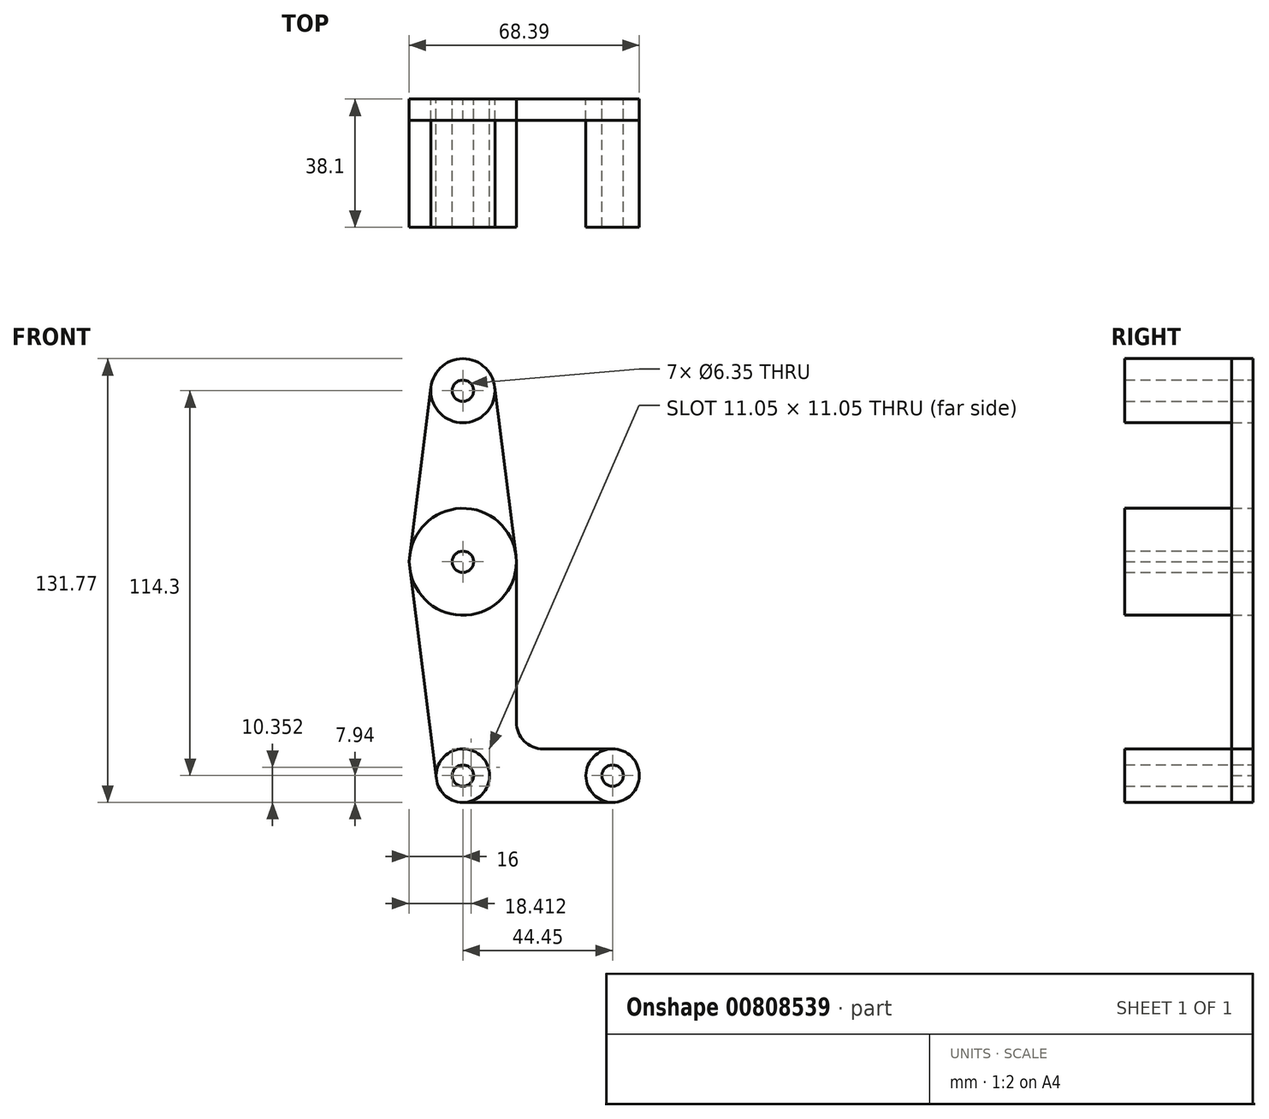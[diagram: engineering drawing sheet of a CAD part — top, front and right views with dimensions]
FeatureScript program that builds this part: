
annotation { "Feature Type Name" : "Feature", "Feature Type Description" : "" }
export const myFeature = defineFeature(function(context is Context, id is Id, definition is map)
    precondition{}
    {
        {
            var Q0;
            Q0=qCreatedBy(makeId("Front.planeOp"),FACE);
            var sketch = newSketch(context, id + "F0", { "sketchPlane" : qUnion([Q0])});
            skCircle(sketch, "E0", {"center": v(0, 0) * mm, "radius": 15.88 * mm});
            skLineSegment(sketch, "E1", {"start": v(0, 0) * mm, "end": v(0, -63.5) * mm});
            skLineSegment(sketch, "E2", {"start": v(0, 0) * mm, "end": v(0, 50.8) * mm});
            skCircle(sketch, "E3", {"center": v(0, 50.8) * mm, "radius": 9.53 * mm});
            skCircle(sketch, "E4", {"center": v(0, -63.5) * mm, "radius": 7.94 * mm});
            skCircle(sketch, "E5", {"center": v(0, 0) * mm, "radius": 3.18 * mm});
            skCircle(sketch, "E6", {"center": v(0, 50.8) * mm, "radius": 3.18 * mm});
            skCircle(sketch, "E7", {"center": v(0, -63.5) * mm, "radius": 3.18 * mm});
            skLineSegment(sketch, "E8", {"start": v(0, -63.5) * mm, "end": v(44.45, -63.5) * mm});
            skCircle(sketch, "E9", {"center": v(44.45, -63.5) * mm, "radius": 7.94 * mm});
            skCircle(sketch, "E10", {"center": v(44.45, -63.5) * mm, "radius": 3.18 * mm});
            skLineSegment(sketch, "E11", {"start": v(44.45, -55.56) * mm, "end": v(23.81, -55.56) * mm});
            skLineSegment(sketch, "E12", {"start": v(-9.45, 52) * mm, "end": v(-16, 0) * mm});
            skLineSegment(sketch, "E13", {"start": v(15.88, 0) * mm, "end": v(15.88, -47.62) * mm});
            skLineSegment(sketch, "E14", {"start": v(-16, 0) * mm, "end": v(-7.88, -64.5) * mm});
            skLineSegment(sketch, "E15", {"start": v(9.45, 52) * mm, "end": v(16, 0) * mm});
            skLineSegment(sketch, "E16", {"start": v(0, -71.44) * mm, "end": v(44.45, -71.44) * mm});
            skPoint(sketch, "E17.visualSharp", {"position": v(15.88, -55.56) * mm});
            skArc(sketch, "E17.filletArc", {"start": v(15.88, -47.62) * mm, "mid": v(18.2, -53.24) * mm, "end": v(23.81, -55.56) * mm});
            skSolve(sketch);
        }
        {
            var Q0;
            {var subQ0=sQuery(id+"F0.wireOp",EDGE,"E12");var subQ1=sQuery(id+"F0.wireOp",EDGE,"E0");var subQ2=makeQuery(id+"F0.imprint","INTERSECT",VERTEX,{"derivedFrom":[subQ1,subQ0]});Q0=makeQuery(id+"F0.imprint","IMPRINT",FACE,{"disambiguationData":[TD([[makeQuery(id+"F0.imprint","IMPRINT",EDGE,{"disambiguationData":[TD([[subQ2,-1.0]])],"derivedFrom":subQ1}),-1.0]])]});}
            var Q1;
            Q1=makeQuery(id+"F0.imprint","IMPRINT",FACE,{"disambiguationData":[TD([[makeQuery(id+"F0.imprint","IMPRINT",EDGE,{"derivedFrom":sQuery(id+"F0.wireOp",EDGE,"E6")}),-1.0]])]});
            var Q2;
            Q2=makeQuery(id+"F0.imprint","IMPRINT",FACE,{"disambiguationData":[TD([[makeQuery(id+"F0.imprint","IMPRINT",EDGE,{"derivedFrom":sQuery(id+"F0.wireOp",EDGE,"E10")}),-1.0]])]});
            var Q3;
            {var subQ0=sQuery(id+"F0.wireOp",EDGE,"E4");var subQ3=sQuery(id+"F0.wireOp",EDGE,"E1");var subQ4=makeQuery(id+"F0.imprint","INTERSECT",VERTEX,{"derivedFrom":[subQ3,subQ0]});Q3=makeQuery(id+"F0.imprint","IMPRINT",FACE,{"disambiguationData":[TD([[makeQuery(id+"F0.imprint","IMPRINT",EDGE,{"disambiguationData":[TD([[subQ4,-1.0]])],"derivedFrom":subQ3}),-1.0]])]});}
            var Q4;
            {var subQ0=sQuery(id+"F0.wireOp",EDGE,"E4");var subQ1=sQuery(id+"F0.wireOp",EDGE,"E1");var subQ2=makeQuery(id+"F0.imprint","INTERSECT",VERTEX,{"derivedFrom":[subQ1,subQ0]});Q4=makeQuery(id+"F0.imprint","IMPRINT",FACE,{"disambiguationData":[TD([[makeQuery(id+"F0.imprint","IMPRINT",EDGE,{"disambiguationData":[TD([[subQ2,-1.0]])],"derivedFrom":subQ1}),1.0]])]});}
            var Q5;
            {var subQ1=sQuery(id+"F0.wireOp",EDGE,"E0");var subQ9=makeQuery(id+"F0.imprint","INTERSECT",VERTEX,{"derivedFrom":[subQ1,sQuery(id+"F0.wireOp",EDGE,"E13")]});Q5=makeQuery(id+"F0.imprint","IMPRINT",FACE,{"disambiguationData":[TD([[makeQuery(id+"F0.imprint","IMPRINT",EDGE,{"disambiguationData":[TD([[subQ9,-1.0]])],"derivedFrom":subQ1}),1.0]])]});}
            var Q6;
            {var subQ0=sQuery(id+"F0.wireOp",EDGE,"E0");var subQ4=makeQuery(id+"F0.imprint","INTERSECT",VERTEX,{"derivedFrom":[subQ0,sQuery(id+"F0.wireOp",EDGE,"E12")]});Q6=makeQuery(id+"F0.imprint","IMPRINT",FACE,{"disambiguationData":[TD([[makeQuery(id+"F0.imprint","IMPRINT",EDGE,{"disambiguationData":[TD([[subQ4,1.0]])],"derivedFrom":subQ0}),1.0]])]});}
            extrude(context, id + "F1", {"entities" : qUnion([Q0, Q1, Q2, Q3, Q4, Q5, Q6]), "depth" : 38.1 * mm, "offsetDistance" : 25.4 * mm});
        }
        {
            var Q0;
            Q0 = qSketchRegion(id + "F0", true);
            extrude(context, id + "F2", {"entities" : qUnion([Q0]), "depth" : 6.35 * mm, "offsetDistance" : 25.4 * mm});
        }
    });
